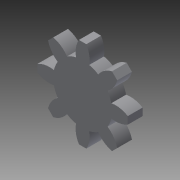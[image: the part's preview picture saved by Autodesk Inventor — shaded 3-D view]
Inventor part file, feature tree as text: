
AUTODESK INVENTOR PART (.ipt)
format: ipt  version: 2013 (Build 170138000, 138)  size: 124,928 bytes
history: native  units: in
note: dims shown in document units (in); Inventor stores cm internally (conversion verified against a paired STEP export)
features: extrude x1, sketch x1
ambient origin geometry x8: Origin, YZ Plane, XZ Plane, XY Plane, X Axis, Y Axis, Z Axis, Center Point
feature tree (2):
  extrude  "Extrusion2"  Depth=0.1in
  sketch  "Sketch2"  dims[d11=0.0312in d13=0.1in d14=0.5497in d15=0.071in d16=3.1496in d18=360.0deg d20=0.0413in d21=0.0625in d22=0.0in]
